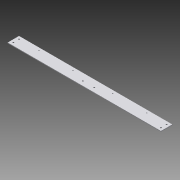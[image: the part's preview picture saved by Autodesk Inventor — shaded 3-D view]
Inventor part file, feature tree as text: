
AUTODESK INVENTOR PART (.ipt)
format: ipt  version: 2015 SP1 (Build 190203100, 203)  size: 199,680 bytes
history: native  units: in
note: dims shown in document units (in); Inventor stores cm internally (conversion verified against a paired STEP export)
features: sketch x7, hole x5, extrude x2, chamfer x1
ambient origin geometry x8: Origin, YZ Plane, XZ Plane, XY Plane, X Axis, Y Axis, Z Axis, Center Point
bodies: Solid1 (feature_tree)
feature tree (15):
  extrude  "Extrusion1"  Depth=2.0in
  sketch  "Sketch2"  dims[d2=2.0in d3=0.125in]
  hole  "Hole2"  [1 undecoded]
  hole  "Hole3"  [1 undecoded]
  extrude  "Extrusion3"  Depth=13.0in
  chamfer  "Chamfer1"  Distance=0.5in
  hole  "Hole5"  [1 undecoded]
  hole  "Hole6"  [1 undecoded]
  hole  "Hole7"  [1 undecoded]
  sketch  "Sketch1"  dims[d0=0.125in d1=2.0in]
  sketch  "Sketch3"  dims[d4=27.0in d5=0.0in d6=4.875in]
  sketch  "Sketch4"  dims[d7=5.875in d8=13.0in]
  sketch  "Sketch6"  dims[d9=0.5in]
  sketch  "Sketch8"  dims[d10=0.5in]
  sketch  "Sketch9"  dims[d11=0.5in d19=0.5in d20=0.5in d21=0.5in d22=0.5in d23=0.75in d24=0.75in d25=0.5in d26=0.5in d27=0.5in d28=0.5in d29=12.5in d30=12.5in d31=0.25in d32=0.75in d33=0.375in d34=0.25in d35=0.5635in d36=1.0in d37=0.8108in d38=4.0in d39=10.0in d40=10.0in d41=4.0in d42=0.5in d43=0.5in d44=0.5in d45=0.5in d46=0.1875in d47=0.75in d48=0.375in d49=0.25in d50=0.5635in d51=1.0in d52=0.8108in d65=6.0in d66=1.0in d67=6.0in d68=1.0in d69=45.0deg d70=135.0deg d71=1.0in d72=0.0in d73=0.125in d74=0.125in d75=45.0deg d91=0.5in d92=0.5in d93=0.5in d94=0.5in d95=4.0in d96=10.0in d97=17.0in d98=23.0in d99=0.1875in d100=0.75in d101=0.375in d102=0.25in d103=0.5635in d104=1.0in d105=0.8108in d106=8.0in d107=0.25in d108=0.25in d109=8.0in d110=0.375in d111=0.75in d112=0.375in d113=0.25in d114=0.5635in d115=1.0in d116=0.8108in d117=0.5in d118=0.5in d119=1.5in d120=0.5in d121=0.5in d122=0.5in d123=0.125in d124=0.75in d125=0.375in d126=0.25in d127=0.5635in d128=1.0in d129=0.8108in]
note: 5 required parameter values undecoded (feature->parameter linkage not recoverable at this tier; creation-order binding heuristic only, values carry confidence <= 0.55)
